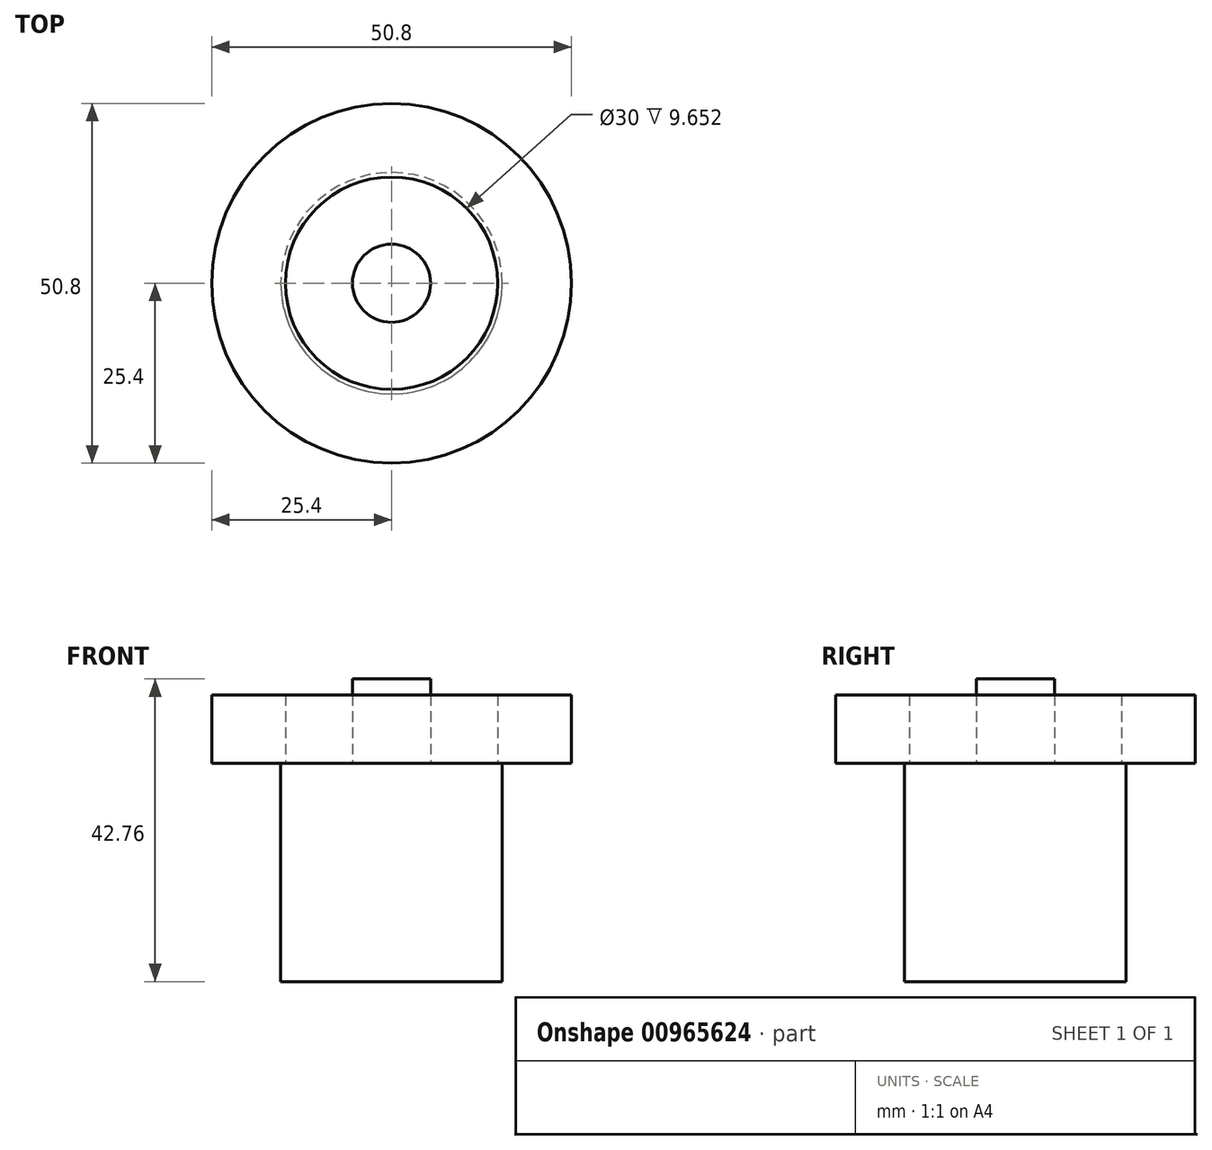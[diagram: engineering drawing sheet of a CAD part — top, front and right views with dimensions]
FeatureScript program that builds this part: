
annotation { "Feature Type Name" : "Feature", "Feature Type Description" : "" }
export const myFeature = defineFeature(function(context is Context, id is Id, definition is map)
    precondition{}
    {
        {
            var Q0;
            Q0=qCreatedBy(makeId("Top.planeOp"),FACE);
            var sketch = newSketch(context, id + "F0", { "sketchPlane" : qUnion([Q0])});
            skCircle(sketch, "E0", {"center": v(0, 0) * mm, "radius": 25.4 * mm});
            skCircle(sketch, "E1", {"center": v(0, 0) * mm, "radius": 15 * mm});
            skSolve(sketch);
        }
        {
            var Q0;
            Q0 = qSketchRegion(id + "F0", true);
            var Q1;
            Q1=makeQuery(id+"F0.imprint","IMPRINT",FACE,{"disambiguationData":[TD([[makeQuery(id+"F0.imprint","IMPRINT",EDGE,{"derivedFrom":sQuery(id+"F0.wireOp",EDGE,"E0")}),1.0]])]});
            extrude(context, id + "F1", {"entities" : qUnion([Q0, Q1]), "depth" : 9.65 * mm, "offsetDistance" : 25.4 * mm});
        }
        {
            var Q0;
            Q0=qCreatedBy(makeId("Front.planeOp"),FACE);
            var sketch = newSketch(context, id + "F2", { "sketchPlane" : qUnion([Q0])});
            skLineSegment(sketch, "E2", {"start": v(0, 11.92) * mm, "end": v(-5.52, 11.92) * mm});
            skLineSegment(sketch, "E3", {"start": v(-5.52, 11.92) * mm, "end": v(-5.52, 0) * mm});
            skLineSegment(sketch, "E4", {"start": v(-5.52, 0) * mm, "end": v(-15.65, 0) * mm});
            skLineSegment(sketch, "E5", {"start": v(-15.65, 0) * mm, "end": v(-15.65, -30.84) * mm});
            skLineSegment(sketch, "E6", {"start": v(-15.65, -30.84) * mm, "end": v(0, -30.84) * mm});
            skLineSegment(sketch, "E7", {"start": v(0, -30.84) * mm, "end": v(0, 11.92) * mm});
            skSolve(sketch);
        }
        {
            var Q0;
            Q0=makeQuery(id+"F2.imprint","IMPRINT",FACE,{"disambiguationData":[TD([[makeQuery(id+"F2.imprint","IMPRINT",EDGE,{"derivedFrom":sQuery(id+"F2.wireOp",EDGE,"E2")}),1.0]])]});
            var Q1;
            Q1=sQuery(id+"F2.wireOp",EDGE,"E7");
            revolve(context, id + "F3", {"operationType" : NewBodyOperationType.ADD, "surfaceOperationType" : NewSurfaceOperationType.NEW, "entities" : qUnion([Q0]), "axis" : qUnion([Q1]), "revolveType" : RevolveType.FULL});
        }
    });
